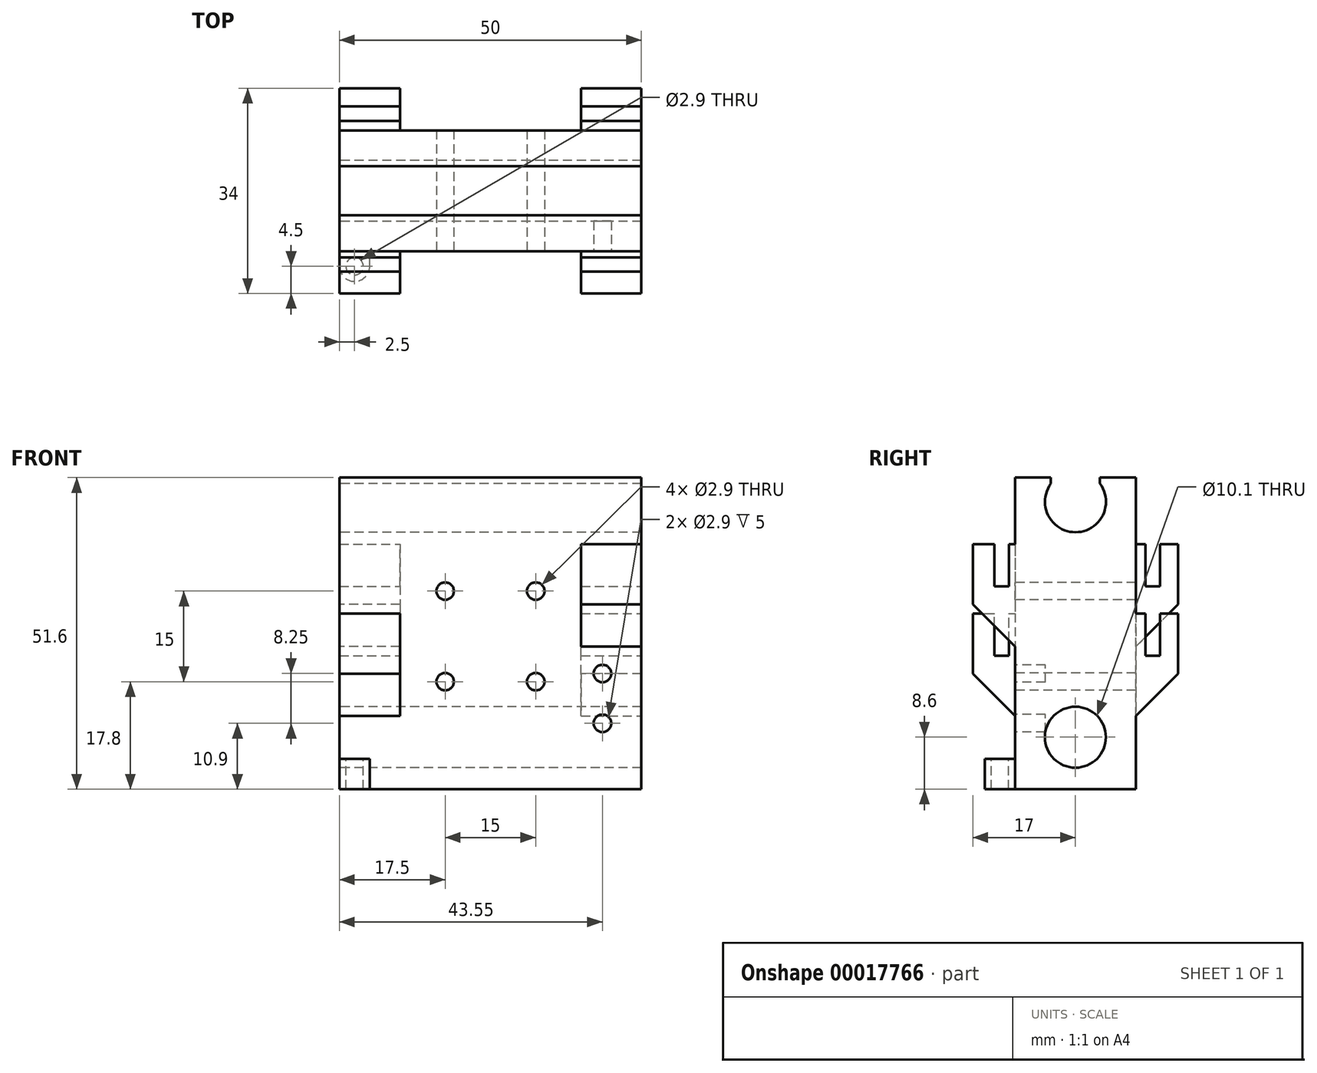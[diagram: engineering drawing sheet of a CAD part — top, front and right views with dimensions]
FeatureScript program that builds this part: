
annotation { "Feature Type Name" : "Feature", "Feature Type Description" : "" }
export const myFeature = defineFeature(function(context is Context, id is Id, definition is map)
    precondition{}
    {
        {
            var Q0;
            Q0=qCreatedBy(makeId("Top.planeOp"),FACE);
            var sketch = newSketch(context, id + "F0", { "sketchPlane" : qUnion([Q0])});
            skLineSegment(sketch, "E0.bottom", {"start": v(0, 0) * mm, "end": v(50, 0) * mm});
            skLineSegment(sketch, "E0.top", {"start": v(0, 20) * mm, "end": v(50, 20) * mm});
            skLineSegment(sketch, "E0.left", {"start": v(0, 0) * mm, "end": v(0, 20) * mm});
            skLineSegment(sketch, "E0.right", {"start": v(50, 0) * mm, "end": v(50, 20) * mm});
            skSolve(sketch);
        }
        {
            var Q0;
            Q0=qSketchRegion(id+"F0",true);
            extrude(context, id + "F1", {"entities" : qUnion([Q0]), "depth" : 50.6 * mm});
        }
        {
            var Q0;
            Q0=makeQuery(id+"F1.opExtrude","SWEPT_FACE",FACE,{"disambiguationData":[OSD([sQuery(id+"F0.wireOp",EDGE,"E0.left")])]});
            var sketch = newSketch(context, id + "F2", { "sketchPlane" : qUnion([Q0])});
            skCircle(sketch, "E1", {"center": v(-10, 8.6) * mm, "radius": 5.05 * mm});
            skCircle(sketch, "E2", {"center": v(-10, 47.6) * mm, "radius": 5.05 * mm});
            skLineSegment(sketch, "E3", {"start": v(-20, 47.6) * mm, "end": v(0, 47.6) * mm, "construction": true});
            skLineSegment(sketch, "E4", {"start": v(-20, 8.6) * mm, "end": v(0, 8.6) * mm, "construction": true});
            skLineSegment(sketch, "E5", {"start": v(-10, 8.6) * mm, "end": v(-10, 0) * mm, "construction": true});
            skLineSegment(sketch, "E6", {"start": v(-10.5, 0) * mm, "end": v(-10.5, 3.57) * mm});
            skLineSegment(sketch, "E7", {"start": v(-9.5, 3.57) * mm, "end": v(-9.5, 0) * mm});
            skLineSegment(sketch, "E8", {"start": v(-10, 13.65) * mm, "end": v(-10, 15.6) * mm});
            skSolve(sketch);
        }
        {
            var Q0;
            {var subQ0=sQuery(id+"F2.wireOp",EDGE,"61a55092-bd36-442a-954f-b1d305e603b2");var subQ1=sQuery(id+"F2.wireOp",EDGE,"E1");var subQ3=makeQuery(id+"F2.imprint","INTERSECT",VERTEX,{"disambiguationData":[OD(0.0)],"derivedFrom":[subQ1,subQ0]});Q0=makeQuery(id+"F2.imprint","IMPRINT",FACE,{"disambiguationData":[TD([[makeQuery(id+"F2.imprint","IMPRINT",EDGE,{"disambiguationData":[TD([[subQ3,-1.0]])],"derivedFrom":subQ1}),1.0]])]});}
            var Q1;
            {var subQ0=sQuery(id+"F2.wireOp",EDGE,"ccdeb851-c584-4ba8-b480-4501c20c5f95");var subQ1=sQuery(id+"F2.wireOp",EDGE,"E1");var subQ3=makeQuery(id+"F2.imprint","INTERSECT",VERTEX,{"disambiguationData":[OD(0.0)],"derivedFrom":[subQ1,subQ0]});Q1=makeQuery(id+"F2.imprint","IMPRINT",FACE,{"disambiguationData":[TD([[makeQuery(id+"F2.imprint","IMPRINT",EDGE,{"disambiguationData":[TD([[subQ3,1.0]])],"derivedFrom":subQ1}),1.0]])]});}
            var Q2;
            Q2=makeQuery(id+"F2.imprint","IMPRINT",FACE,{"disambiguationData":[TD([[makeQuery(id+"F2.imprint","IMPRINT",EDGE,{"derivedFrom":sQuery(id+"F2.wireOp",EDGE,"2eafa571-adb2-4dce-9d5a-bde4304df95e")}),-1.0]])]});
            var Q3;
            {var subQ0=sQuery(id+"F2.wireOp",EDGE,"e375dc4c-f3f4-4a37-bcef-8904ddf818ad");Q3=makeQuery(id+"F2.imprint","IMPRINT",FACE,{"disambiguationData":[TD([[makeQuery(id+"F2.imprint","IMPRINT",EDGE,{"derivedFrom":subQ0}),-1.0]])]});}
            var Q4;
            {var subQ3=sQuery(id+"F2.wireOp",EDGE,"E8");Q4=makeQuery(id+"F2.imprint","IMPRINT",FACE,{"disambiguationData":[TD([[makeQuery(id+"F2.imprint","IMPRINT",EDGE,{"derivedFrom":subQ3}),-1.0]])]});}
            var Q5;
            {var subQ3=sQuery(id+"F2.wireOp",EDGE,"E8");Q5=makeQuery(id+"F2.imprint","IMPRINT",FACE,{"disambiguationData":[TD([[makeQuery(id+"F2.imprint","IMPRINT",EDGE,{"derivedFrom":subQ3}),1.0]])]});}
            var Q6;
            {var subQ7=sQuery(id+"F2.wireOp",EDGE,"e375dc4c-f3f4-4a37-bcef-8904ddf818ad");Q6=makeQuery(id+"F2.imprint","IMPRINT",FACE,{"disambiguationData":[TD([[makeQuery(id+"F2.imprint","IMPRINT",EDGE,{"derivedFrom":subQ7}),1.0]])]});}
            var Q7;
            {var subQ3=sQuery(id+"F2.wireOp",EDGE,"deb4647e-459a-4bd0-b85b-410e59fd364d");Q7=makeQuery(id+"F2.imprint","IMPRINT",FACE,{"disambiguationData":[TD([[makeQuery(id+"F2.imprint","IMPRINT",EDGE,{"derivedFrom":subQ3}),-1.0]])]});}
            var Q8;
            {var subQ0=sQuery(id+"F2.wireOp",EDGE,"1f1fe5f8-645c-480d-a2d4-7acea15178eb");Q8=makeQuery(id+"F2.imprint","IMPRINT",FACE,{"disambiguationData":[TD([[makeQuery(id+"F2.imprint","IMPRINT",EDGE,{"derivedFrom":subQ0}),1.0]])]});}
            var Q9;
            {var subQ0=sQuery(id+"F2.wireOp",EDGE,"1f1fe5f8-645c-480d-a2d4-7acea15178eb");Q9=makeQuery(id+"F2.imprint","IMPRINT",FACE,{"disambiguationData":[TD([[makeQuery(id+"F2.imprint","IMPRINT",EDGE,{"derivedFrom":subQ0}),1.0]])]});}
            var Q10;
            {var subQ3=sQuery(id+"F2.wireOp",EDGE,"deb4647e-459a-4bd0-b85b-410e59fd364d");Q10=makeQuery(id+"F2.imprint","IMPRINT",FACE,{"disambiguationData":[TD([[makeQuery(id+"F2.imprint","IMPRINT",EDGE,{"derivedFrom":subQ3}),-1.0]])]});}
            var Q11;
            {var subQ1=sQuery(id+"F2.wireOp",EDGE,"E2");var subQ4=makeQuery(id+"F2.imprint","INTERSECT",VERTEX,{"derivedFrom":[subQ1,sQuery(id+"F2.wireOp",EDGE,"deb4647e-459a-4bd0-b85b-410e59fd364d")]});Q11=makeQuery(id+"F2.imprint","IMPRINT",FACE,{"disambiguationData":[TD([[makeQuery(id+"F2.imprint","IMPRINT",EDGE,{"disambiguationData":[TD([[subQ4,-1.0]])],"derivedFrom":subQ1}),1.0]])]});}
            extrude(context, id + "F3", {"entities" : qUnion([Q0, Q1, Q2, Q3, Q4, Q5, Q6, Q7, Q8, Q9, Q10, Q11]), "operationType" : NewBodyOperationType.REMOVE, "endBound" : BoundingType.THROUGH_ALL, "oppositeDirection" : true, "depth" : 25 * mm});
        }
        {
            var Q0;
            Q0=makeQuery(id+"F1.opExtrude","SWEPT_FACE",FACE,{"disambiguationData":[OSD([sQuery(id+"F0.wireOp",EDGE,"E0.bottom")])]});
            var sketch = newSketch(context, id + "F4", { "sketchPlane" : qUnion([Q0])});
            skLineSegment(sketch, "E9.bottom", {"start": v(0, 29.1) * mm, "end": v(10, 29.1) * mm});
            skLineSegment(sketch, "E9.top", {"start": v(0, 9.1) * mm, "end": v(10, 9.1) * mm});
            skLineSegment(sketch, "E9.left", {"start": v(0, 29.1) * mm, "end": v(0, 9.1) * mm});
            skLineSegment(sketch, "E9.right", {"start": v(10, 29.1) * mm, "end": v(10, 9.1) * mm});
            skLineSegment(sketch, "E10.bottom", {"start": v(50, 40.6) * mm, "end": v(40, 40.6) * mm});
            skLineSegment(sketch, "E10.top", {"start": v(50, 20.6) * mm, "end": v(40, 20.6) * mm});
            skLineSegment(sketch, "E10.left", {"start": v(50, 40.6) * mm, "end": v(50, 20.6) * mm});
            skLineSegment(sketch, "E10.right", {"start": v(40, 40.6) * mm, "end": v(40, 20.6) * mm});
            skPoint(sketch, "E11", {"position": v(0, 47.6) * mm});
            skPoint(sketch, "E12", {"position": v(0, 8.6) * mm});
            skSolve(sketch);
        }
        {
            var Q0;
            Q0=qSketchRegion(id+"F4",true);
            extrude(context, id + "F5", {"entities" : qUnion([Q0]), "operationType" : NewBodyOperationType.ADD, "depth" : 7 * mm});
        }
        {
            var Q0;
            Q0=makeQuery(id+"F5.opExtrude","CAP_EDGE",EDGE,{"disambiguationData":[OSD([sQuery(id+"F4.wireOp",EDGE,"E9.top")])],"isStart":false});
            var Q1;
            Q1=makeQuery(id+"F5.opExtrude","CAP_EDGE",EDGE,{"disambiguationData":[OSD([sQuery(id+"F4.wireOp",EDGE,"E10.top")])],"isStart":false});
            chamfer(context, id + "F6", {"entities" : qUnion([Q0, Q1]), "width" : 10 * mm, "tangentPropagation" : true});
        }
        {
            var Q0;
            Q0=makeQuery(id+"F5.opExtrude","SWEPT_FACE",FACE,{"disambiguationData":[OSD([sQuery(id+"F4.wireOp",EDGE,"E9.bottom")])]});
            var sketch = newSketch(context, id + "F7", { "sketchPlane" : qUnion([Q0])});
            skLineSegment(sketch, "E13", {"start": v(-935.9, 0) * mm, "end": v(-935.88, -4.54) * mm});
            skLineSegment(sketch, "E14", {"start": v(0, -3.4) * mm, "end": v(10, -3.4) * mm});
            skLineSegment(sketch, "E15", {"start": v(0, -3.4) * mm, "end": v(0, -1) * mm});
            skLineSegment(sketch, "E16", {"start": v(0, -1) * mm, "end": v(10, -1) * mm});
            skLineSegment(sketch, "E17", {"start": v(10, -1) * mm, "end": v(10, -3.4) * mm});
            skSolve(sketch);
        }
        {
            var Q0;
            Q0=qSketchRegion(id+"F7",true);
            extrude(context, id + "F8", {"entities" : qUnion([Q0]), "operationType" : NewBodyOperationType.REMOVE, "oppositeDirection" : true, "depth" : 7 * mm});
        }
        {
            var Q0;
            Q0=makeQuery(id+"F5.opExtrude","SWEPT_FACE",FACE,{"disambiguationData":[OSD([sQuery(id+"F4.wireOp",EDGE,"E10.bottom")])]});
            var sketch = newSketch(context, id + "F9", { "sketchPlane" : qUnion([Q0])});
            skLineSegment(sketch, "E18", {"start": v(40, -3.4) * mm, "end": v(50, -3.4) * mm});
            skLineSegment(sketch, "E19", {"start": v(-711.83, -0.3) * mm, "end": v(-711.8, -4.83) * mm});
            skLineSegment(sketch, "E20", {"start": v(224.08, -3.7) * mm, "end": v(234.08, -3.7) * mm});
            skLineSegment(sketch, "E21", {"start": v(224.08, -3.7) * mm, "end": v(224.08, -1.3) * mm});
            skLineSegment(sketch, "E22", {"start": v(224.08, -1.3) * mm, "end": v(234.08, -1.3) * mm});
            skLineSegment(sketch, "E23", {"start": v(234.08, -1.3) * mm, "end": v(234.08, -3.7) * mm});
            skLineSegment(sketch, "E24", {"start": v(-708.88, -0.88) * mm, "end": v(-708.85, -5.41) * mm});
            skLineSegment(sketch, "E25", {"start": v(227.03, -4.28) * mm, "end": v(237.03, -4.28) * mm});
            skLineSegment(sketch, "E26", {"start": v(227.03, -4.28) * mm, "end": v(227.03, -1.88) * mm});
            skLineSegment(sketch, "E27", {"start": v(227.03, -1.88) * mm, "end": v(237.03, -1.88) * mm});
            skLineSegment(sketch, "E28", {"start": v(237.03, -1.88) * mm, "end": v(237.03, -4.28) * mm});
            skLineSegment(sketch, "E29", {"start": v(40, -3.4) * mm, "end": v(40, -1) * mm});
            skLineSegment(sketch, "E30", {"start": v(40, -1) * mm, "end": v(50, -1) * mm});
            skLineSegment(sketch, "E31", {"start": v(50, -1) * mm, "end": v(50, -3.4) * mm});
            skSolve(sketch);
        }
        {
            var Q0;
            Q0=qSketchRegion(id+"F9",true);
            extrude(context, id + "F10", {"entities" : qUnion([Q0]), "operationType" : NewBodyOperationType.REMOVE, "oppositeDirection" : true, "depth" : 7 * mm});
        }
        {
            var Q0;
            Q0=makeQuery(id+"F1.opExtrude","SWEPT_FACE",FACE,{"disambiguationData":[OSD([sQuery(id+"F0.wireOp",EDGE,"E0.top")])]});
            var sketch = newSketch(context, id + "F11", { "sketchPlane" : qUnion([Q0])});
            skLineSegment(sketch, "E32.bottom", {"start": v(-50, 9.1) * mm, "end": v(-40, 9.1) * mm});
            skLineSegment(sketch, "E32.top", {"start": v(-50, 29.1) * mm, "end": v(-40, 29.1) * mm});
            skLineSegment(sketch, "E32.left", {"start": v(-50, 9.1) * mm, "end": v(-50, 29.1) * mm});
            skLineSegment(sketch, "E32.right", {"start": v(-40, 9.1) * mm, "end": v(-40, 29.1) * mm});
            skLineSegment(sketch, "E33.bottom", {"start": v(0, 40.6) * mm, "end": v(-10, 40.6) * mm});
            skLineSegment(sketch, "E33.top", {"start": v(0, 20.6) * mm, "end": v(-10, 20.6) * mm});
            skLineSegment(sketch, "E33.left", {"start": v(0, 40.6) * mm, "end": v(0, 20.6) * mm});
            skLineSegment(sketch, "E33.right", {"start": v(-10, 40.6) * mm, "end": v(-10, 20.6) * mm});
            skSolve(sketch);
        }
        {
            var Q0;
            Q0=qSketchRegion(id+"F11",true);
            extrude(context, id + "F12", {"entities" : qUnion([Q0]), "operationType" : NewBodyOperationType.ADD, "depth" : 7 * mm});
        }
        {
            var Q0;
            Q0=makeQuery(id+"F12.opExtrude","SWEPT_FACE",FACE,{"disambiguationData":[OSD([sQuery(id+"F11.wireOp",EDGE,"E32.top")])]});
            var sketch = newSketch(context, id + "F13", { "sketchPlane" : qUnion([Q0])});
            skLineSegment(sketch, "E34", {"start": v(40, 21.6) * mm, "end": v(50, 21.6) * mm});
            skLineSegment(sketch, "E35", {"start": v(40, 21.6) * mm, "end": v(40, 24) * mm});
            skLineSegment(sketch, "E36", {"start": v(40, 24) * mm, "end": v(50, 24) * mm});
            skLineSegment(sketch, "E37", {"start": v(50, 24) * mm, "end": v(50, 21.6) * mm});
            skSolve(sketch);
        }
        {
            var Q0;
            Q0=makeQuery(id+"F13.imprint","IMPRINT",FACE,{"disambiguationData":[TD([[makeQuery(id+"F13.imprint","IMPRINT",EDGE,{"derivedFrom":sQuery(id+"F13.wireOp",EDGE,"E34")}),1.0]])]});
            extrude(context, id + "F14", {"entities" : qUnion([Q0]), "operationType" : NewBodyOperationType.REMOVE, "oppositeDirection" : true, "depth" : 7 * mm});
        }
        {
            var Q0;
            Q0=makeQuery(id+"F12.opExtrude","SWEPT_FACE",FACE,{"disambiguationData":[OSD([sQuery(id+"F11.wireOp",EDGE,"E33.bottom")])]});
            var sketch = newSketch(context, id + "F15", { "sketchPlane" : qUnion([Q0])});
            skLineSegment(sketch, "E38", {"start": v(0, 21.6) * mm, "end": v(10, 21.6) * mm});
            skLineSegment(sketch, "E39", {"start": v(0, 21.6) * mm, "end": v(0, 24) * mm});
            skLineSegment(sketch, "E40", {"start": v(0, 24) * mm, "end": v(10, 24) * mm});
            skLineSegment(sketch, "E41", {"start": v(10, 24) * mm, "end": v(10, 21.6) * mm});
            skSolve(sketch);
        }
        {
            var Q0;
            Q0=makeQuery(id+"F15.imprint","IMPRINT",FACE,{"disambiguationData":[TD([[makeQuery(id+"F15.imprint","IMPRINT",EDGE,{"derivedFrom":sQuery(id+"F15.wireOp",EDGE,"E38")}),1.0]])]});
            extrude(context, id + "F16", {"entities" : qUnion([Q0]), "operationType" : NewBodyOperationType.REMOVE, "oppositeDirection" : true, "depth" : 7 * mm});
        }
        {
            var Q0;
            Q0=makeQuery(id+"F12.opExtrude","CAP_EDGE",EDGE,{"disambiguationData":[OSD([sQuery(id+"F11.wireOp",EDGE,"E33.top")])],"isStart":false});
            var Q1;
            Q1=makeQuery(id+"F12.opExtrude","CAP_EDGE",EDGE,{"disambiguationData":[OSD([sQuery(id+"F11.wireOp",EDGE,"E32.bottom")])],"isStart":false});
            chamfer(context, id + "F17", {"entities" : qUnion([Q0, Q1]), "width" : 10 * mm, "tangentPropagation" : true});
        }
        {
            var Q0;
            Q0=makeQuery(id+"F1.opExtrude","SWEPT_FACE",FACE,{"disambiguationData":[OSD([sQuery(id+"F0.wireOp",EDGE,"E0.bottom")])]});
            var sketch = newSketch(context, id + "F18", { "sketchPlane" : qUnion([Q0])});
            skCircle(sketch, "E42", {"center": v(17.5, 32.8) * mm, "radius": 1.45 * mm});
            skCircle(sketch, "E43", {"center": v(32.5, 32.8) * mm, "radius": 1.45 * mm});
            skCircle(sketch, "E44", {"center": v(17.5, 17.8) * mm, "radius": 1.45 * mm});
            skCircle(sketch, "E45", {"center": v(32.5, 17.8) * mm, "radius": 1.45 * mm});
            skLineSegment(sketch, "E46", {"start": v(17.5, 32.8) * mm, "end": v(0, 32.8) * mm});
            skLineSegment(sketch, "E47", {"start": v(32.5, 17.8) * mm, "end": v(50, 17.8) * mm});
            skLineSegment(sketch, "E48", {"start": v(32.5, 32.8) * mm, "end": v(32.5, 50.6) * mm});
            skLineSegment(sketch, "E49", {"start": v(17.5, 17.8) * mm, "end": v(17.5, 0) * mm});
            skLineSegment(sketch, "E50", {"start": v(25, 0) * mm, "end": v(25, 13.82) * mm, "construction": true});
            skSolve(sketch);
        }
        {
            var Q0;
            Q0=qSketchRegion(id+"F18",true);
            var Q1;
            Q1=makeQuery(id+"F18.imprint","IMPRINT",FACE,{"disambiguationData":[TD([[makeQuery(id+"F18.imprint","IMPRINT",EDGE,{"derivedFrom":sQuery(id+"F18.wireOp",EDGE,"E42")}),1.0]])]});
            var Q2;
            Q2=makeQuery(id+"F18.imprint","IMPRINT",FACE,{"disambiguationData":[TD([[makeQuery(id+"F18.imprint","IMPRINT",EDGE,{"derivedFrom":sQuery(id+"F18.wireOp",EDGE,"E43")}),1.0]])]});
            var Q3;
            Q3=makeQuery(id+"F18.imprint","IMPRINT",FACE,{"disambiguationData":[TD([[makeQuery(id+"F18.imprint","IMPRINT",EDGE,{"derivedFrom":sQuery(id+"F18.wireOp",EDGE,"E45")}),1.0]])]});
            var Q4;
            Q4=makeQuery(id+"F18.imprint","IMPRINT",FACE,{"disambiguationData":[TD([[makeQuery(id+"F18.imprint","IMPRINT",EDGE,{"derivedFrom":sQuery(id+"F18.wireOp",EDGE,"E44")}),1.0]])]});
            extrude(context, id + "F19", {"entities" : qUnion([Q0, Q1, Q2, Q3, Q4]), "operationType" : NewBodyOperationType.REMOVE, "endBound" : BoundingType.THROUGH_ALL, "oppositeDirection" : true, "depth" : 25 * mm});
        }
        {
            var Q0;
            Q0=makeQuery(id+"F1.opExtrude","SWEPT_FACE",FACE,{"disambiguationData":[OSD([sQuery(id+"F0.wireOp",EDGE,"E0.bottom")])]});
            var sketch = newSketch(context, id + "F20", { "sketchPlane" : qUnion([Q0])});
            skCircle(sketch, "E51", {"center": v(43.55, 19.15) * mm, "radius": 1.45 * mm});
            skCircle(sketch, "E52", {"center": v(43.55, 10.9) * mm, "radius": 1.45 * mm});
            skSolve(sketch);
        }
        {
            var Q0;
            Q0=qSketchRegion(id+"F20",true);
            extrude(context, id + "F21", {"entities" : qUnion([Q0]), "operationType" : NewBodyOperationType.REMOVE, "oppositeDirection" : true, "depth" : 5 * mm});
        }
        {
            var Q0;
            Q0=makeQuery(id+"F1.opExtrude","SWEPT_FACE",FACE,{"disambiguationData":[OSD([sQuery(id+"F0.wireOp",EDGE,"E0.bottom")])]});
            var sketch = newSketch(context, id + "F22", { "sketchPlane" : qUnion([Q0])});
            skLineSegment(sketch, "E53.bottom", {"start": v(0, 0) * mm, "end": v(5, 0) * mm});
            skLineSegment(sketch, "E53.top", {"start": v(0, 5) * mm, "end": v(5, 5) * mm});
            skLineSegment(sketch, "E53.left", {"start": v(0, 0) * mm, "end": v(0, 5) * mm});
            skLineSegment(sketch, "E53.right", {"start": v(5, 0) * mm, "end": v(5, 5) * mm});
            skSolve(sketch);
        }
        {
            var Q0;
            Q0=qSketchRegion(id+"F22",true);
            extrude(context, id + "F23", {"entities" : qUnion([Q0]), "operationType" : NewBodyOperationType.ADD, "depth" : 5 * mm});
        }
        {
            var Q0;
            Q0=makeQuery(id+"F23.opExtrude","SWEPT_FACE",FACE,{"disambiguationData":[OSD([sQuery(id+"F22.wireOp",EDGE,"E53.top")])]});
            var sketch = newSketch(context, id + "F24", { "sketchPlane" : qUnion([Q0])});
            skCircle(sketch, "E54", {"center": v(2.5, -2.5) * mm, "radius": 1.45 * mm});
            skLineSegment(sketch, "E55", {"start": v(0, -2.5) * mm, "end": v(5, -2.5) * mm});
            skSolve(sketch);
        }
        {
            var Q0;
            Q0=qSketchRegion(id+"F24",true);
            extrude(context, id + "F25", {"entities" : qUnion([Q0]), "operationType" : NewBodyOperationType.REMOVE, "oppositeDirection" : true, "depth" : 25 * mm});
        }
        {
            var Q0;
            Q0=makeQuery(id+"F23.opExtrude","CAP_EDGE",EDGE,{"disambiguationData":[OSD([sQuery(id+"F22.wireOp",EDGE,"E53.left")])],"isStart":false});
            var Q1;
            Q1=makeQuery(id+"F23.opExtrude","CAP_EDGE",EDGE,{"disambiguationData":[OSD([sQuery(id+"F22.wireOp",EDGE,"E53.right")])],"isStart":false});
            fillet(context, id + "F26", {"entities" : qUnion([Q0, Q1]), "radius" : 2.5 * mm, "tangentPropagation" : true, "allowEdgeOverflow" : false});
        }
        {
            var Q0;
            {var subQ0=sQuery(id+"F0.wireOp",EDGE,"E0.top");var subQ1=sQuery(id+"F0.wireOp",EDGE,"E0.left");var subQ2=sQuery(id+"F0.wireOp",EDGE,"E0.right");Q0=makeQuery(id+"F3.boolean.opBoolean","SPLIT",FACE,{"disambiguationData":[TD([makeQuery(id+"F1.opExtrude","SWEPT_FACE",FACE,{"disambiguationData":[OSD([subQ0])]})])],"derivedFrom":makeQuery(id+"F1.opExtrude","CAP_FACE",FACE,{"disambiguationData":[OSD([sQuery(id+"F0.wireOp",EDGE,"E0.bottom"),subQ0,subQ1,subQ2])],"isStart":false})});}
            var Q1;
            {var subQ0=sQuery(id+"F0.wireOp",EDGE,"E0.bottom");var subQ1=sQuery(id+"F0.wireOp",EDGE,"E0.left");var subQ2=sQuery(id+"F0.wireOp",EDGE,"E0.right");Q1=makeQuery(id+"F3.boolean.opBoolean","SPLIT",FACE,{"disambiguationData":[TD([makeQuery(id+"F1.opExtrude","SWEPT_FACE",FACE,{"disambiguationData":[OSD([subQ0])]})])],"derivedFrom":makeQuery(id+"F1.opExtrude","CAP_FACE",FACE,{"disambiguationData":[OSD([subQ0,sQuery(id+"F0.wireOp",EDGE,"E0.top"),subQ1,subQ2])],"isStart":false})});}
            extrude(context, id + "F27", {"entities" : qUnion([Q0, Q1]), "operationType" : NewBodyOperationType.ADD, "depth" : 1 * mm});
        }
    });
